# Revit family: BOS-Eckschutzprofil-Typ-1-3-QD-Q15NbD-MW_Familie
name_source: partatom
category: Türen
revit_build: Autodesk Revit 2017 (Build: 20160225_1515(x64)
units: mm (PartAtom-declared; Revit-internal decimal feet)

## family parameters
Basisbauteil = Wand
Beim Laden mit Abzugskörper schneiden = Nein
Gemeinsam genutzt = Nein
Immer vertikal = Ja
Raumberechnungspunkt = Ja

## types (4) — shared parameters
Allgemeine Informationen zu Stahlzargen = www.BestOfSteel.de/tools-downloads/technische-infos-rund-um-die-stahlzarge/
BE max. = 100 mm  [stored 0.328084 ft]
Bauelement = BOS Eckschutzprofil
Funktion = Innen
GT Gesamttiefe (Typ 3) = 60 mm  [stored 0.19685 ft]
GT max. = 650 mm  [stored 2.13255 ft]
Hersteller = BOS GmbH Best Of Steel, Lütkenfelde 4, D-48282 Emsdetten
Info-Texte sichtbar = Ja
Information in English = Nein
LDB max. = 1311 mm  [stored 4.30118 ft]
LDB min. = 561 mm
LDH max. = 2843 mm  [stored 9.32743 ft]
LDH min. = 1593 mm  [stored 5.22638 ft]
Material = grundiert, feuerverzinktes Feinblech nach DIN EN 10143
Material - Zarge = <Nach Kategorie>
Putzwinkel hinten (QD, Q15NbD) = 25 mm  [stored 0.082021 ft]
URL = www.BestOfSteel.de/stahlzargen/weitere-loesungen/eckschutz-wandabschlussprofile/
zero-valued in all types: Breite, Dicke, Rohbaubreite, Rohbauhöhe

## per-type parameters (varying)
| type | Beschreibung | Einfügepunkt | Logo mittig | Logo unten | Modell | Putzwinkel hinten | Putzwinkel hinten (Typ 1) | Putzwinkel vorne | Q15NbD | QD | Typ 1 | Typ 1 oder QD | Typ 3 | Wandstärke max. (QD, Q15NbD) | Wandstärke min. |
| Eckschutzprofil Q15NbD | Eckschutzprofil QD für Mauerwerk | 32.5 mm  [stored 0.106627 ft] | Ja | Nein | Eckschutzprofil QD | 25 mm  [stored 0.082021 ft] | 25 mm  [stored 0.082021 ft] | 0 mm  [stored 0 ft] | Ja | Nein | Nein | Nein | Nein | 650 mm  [stored 2.13255 ft] | 100 mm  [stored 0.328084 ft] |
| Eckschutzprofil Typ 1 | Eckschutzprofil Typ 1 für Mauerwerk | 30 mm  [stored 0.0984252 ft] | Nein | Ja | Eckschutzprofil Typ 1 | 10 mm  [stored 0.0328084 ft] | 10 mm  [stored 0.0328084 ft] | 10 mm  [stored 0.0328084 ft] | Nein | Nein | Ja | Ja | Nein | 640 mm  [stored 2.09974 ft] | 80 mm  [stored 0.262467 ft] |
| Eckschutzprofil Typ 3 | Eckschutzprofil Typ 3 für Mauerwerk | 20 mm  [stored 0.0656168 ft] | Nein | Ja | Eckschutzprofil Typ 3 | 0 mm  [stored 0 ft] | 10 mm  [stored 0.0328084 ft] | 0 mm  [stored 0 ft] | Nein | Nein | Nein | Nein | Ja | 650 mm  [stored 2.13255 ft] | 100 mm  [stored 0.328084 ft] |
| Eckschutzprofil QD | Eckschutzprofil QD für Mauerwerk | 37 mm  [stored 0.121391 ft] | Ja | Nein | Eckschutzprofil QD | 25 mm  [stored 0.082021 ft] | 25 mm  [stored 0.082021 ft] | 10 mm  [stored 0.0328084 ft] | Nein | Ja | Nein | Ja | Nein | 640 mm  [stored 2.09974 ft] | 100 mm  [stored 0.328084 ft] |

note: [stored X ft] marks values corroborated as IEEE doubles in the binary element streams (Revit-internal decimal feet)
